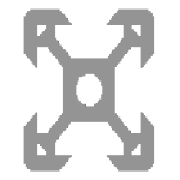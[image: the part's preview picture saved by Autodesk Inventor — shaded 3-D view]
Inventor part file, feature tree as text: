
AUTODESK INVENTOR PART (.ipt)
format: ipt  version: 2019 (Build 230136000, 136)  size: 198,144 bytes
history: native  units: mm
features: other x3, sketch x3, plane x1
ambient origin geometry x8: Origin, YZ Plane, XZ Plane, XY Plane, X Axis, Y Axis, Z Axis, Center Point
bodies: Solid1 (feature_tree), Body (feature_tree)
feature tree (7):
  other  "Driven Length"
  other  "Start Plane"
  other  "End Plane"
  sketch  "Sketch1"  dims[d2=4.2mm]
  sketch  "Sketch4"  dims[d3=1.5mm]
  plane  "Work Plane4"
  sketch  "Sketch5"  dims[d4=1.64mm d5=1.8mm d6=5.68mm d7=1.8mm d9=1.5mm d12=-0.0mm d13=340.0mm d14=0.13mm d15=0.0mm d18=90.0deg d17=340.0mm]
